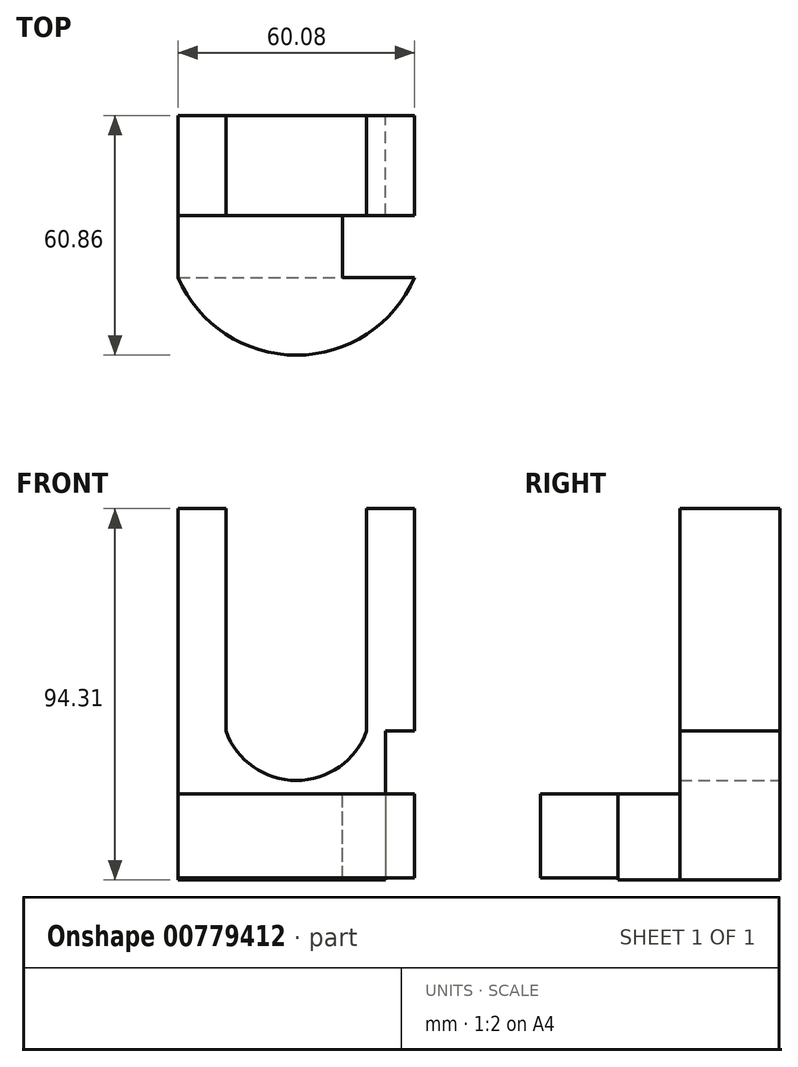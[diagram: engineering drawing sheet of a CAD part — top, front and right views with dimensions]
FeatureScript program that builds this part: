
annotation { "Feature Type Name" : "Feature", "Feature Type Description" : "" }
export const myFeature = defineFeature(function(context is Context, id is Id, definition is map)
    precondition{}
    {
        {
            var Q0;
            Q0=qCreatedBy(makeId("Front.planeOp"),FACE);
            var sketch = newSketch(context, id + "F0", { "sketchPlane" : qUnion([Q0])});
            skLineSegment(sketch, "E0.bottom", {"start": v(-60.08, 56.5) * mm, "end": v(-47.92, 56.5) * mm});
            skLineSegment(sketch, "E0.top", {"start": v(-60.08, -37.8) * mm, "end": v(0, -37.8) * mm});
            skLineSegment(sketch, "E0.left", {"start": v(-60.08, 56.5) * mm, "end": v(-60.08, -37.8) * mm});
            skLineSegment(sketch, "E0.right", {"start": v(0, 56.5) * mm, "end": v(0, -37.8) * mm});
            skLineSegment(sketch, "E1.left", {"start": v(-47.92, 56.5) * mm, "end": v(-47.92, 0) * mm});
            skLineSegment(sketch, "E1.right", {"start": v(-12.16, 56.5) * mm, "end": v(-12.16, 0) * mm});
            skLineSegment(sketch, "E2.trimOffspring", {"start": v(-12.16, 56.5) * mm, "end": v(0, 56.5) * mm});
            skArc(sketch, "E3", {"start": v(-47.92, 0) * mm, "mid": v(-30.04, -12.55) * mm, "end": v(-12.16, 0) * mm});
            skLineSegment(sketch, "E4.bottom", {"start": v(-60.08, -15.91) * mm, "end": v(0, -15.91) * mm});
            skLineSegment(sketch, "E4.left", {"start": v(-60.08, -15.91) * mm, "end": v(-60.08, -37.8) * mm});
            skLineSegment(sketch, "E4.right", {"start": v(0, -15.91) * mm, "end": v(0, -37.8) * mm});
            skSolve(sketch);
        }
        {
            var Q0;
            {var subQ4=sQuery(id+"F0.wireOp",EDGE,"E0.bottom");Q0=makeQuery(id+"F0.imprint","IMPRINT",FACE,{"disambiguationData":[TD([[makeQuery(id+"F0.imprint","IMPRINT",EDGE,{"derivedFrom":subQ4}),-1.0]])]});}
            extrude(context, id + "F1", {"entities" : qUnion([Q0]), "depth" : 25.4 * mm, "offsetDistance" : 25.4 * mm});
        }
        {
            var Q0;
            {var subQ0=sQuery(id+"F0.wireOp",EDGE,"E0.top");Q0=makeQuery(id+"F0.imprint","IMPRINT",FACE,{"disambiguationData":[TD([[makeQuery(id+"F0.imprint","IMPRINT",EDGE,{"derivedFrom":subQ0}),1.0]])]});}
            extrude(context, id + "F2", {"entities" : qUnion([Q0]), "operationType" : NewBodyOperationType.ADD, "depth" : 41.15 * mm, "offsetDistance" : 25.4 * mm});
        }
        {
            var Q0;
            Q0=makeQuery(id+"F2.opExtrude","SWEPT_FACE",FACE,{"disambiguationData":[OSD([sQuery(id+"F0.wireOp",EDGE,"E4.bottom")])]});
            var sketch = newSketch(context, id + "F3", { "sketchPlane" : qUnion([Q0])});
            skArc(sketch, "E5", {"start": v(-60.08, -41.15) * mm, "mid": v(-30.04, -60.86) * mm, "end": v(0, -41.15) * mm});
            skSolve(sketch);
        }
        {
            var Q0;
            Q0=makeQuery(id+"F3.imprint","IMPRINT",FACE,{"disambiguationData":[TD([[makeQuery(id+"F3.imprint","IMPRINT",EDGE,{"derivedFrom":sQuery(id+"F3.wireOp",EDGE,"E5")}),1.0]])]});
            extrude(context, id + "F4", {"entities" : qUnion([Q0]), "operationType" : NewBodyOperationType.ADD, "oppositeDirection" : true, "depth" : 21.34 * mm, "offsetDistance" : 25.4 * mm});
        }
        {
            var Q0;
            {var subQ0=sQuery(id+"F0.wireOp",EDGE,"E0.right");Q0=makeQuery(id+"F2.boolean.opBoolean","MERGE",FACE,{"derivedFrom":[makeQuery(id+"F1.opExtrude","SWEPT_FACE",FACE,{"disambiguationData":[OSD([subQ0])]}),makeQuery(id+"F2.opExtrude","SWEPT_FACE",FACE,{"disambiguationData":[OSD([subQ0])]})]});}
            var sketch = newSketch(context, id + "F5", { "sketchPlane" : qUnion([Q0])});
            skLineSegment(sketch, "E6.bottom", {"start": v(-25.4, 0) * mm, "end": v(0, 0) * mm});
            skLineSegment(sketch, "E6.top", {"start": v(-25.4, -37.8) * mm, "end": v(0, -37.8) * mm});
            skLineSegment(sketch, "E6.left", {"start": v(-25.4, 0) * mm, "end": v(-25.4, -37.8) * mm});
            skLineSegment(sketch, "E6.right", {"start": v(0, 0) * mm, "end": v(0, -37.8) * mm});
            skSolve(sketch);
        }
        {
            var Q0;
            {var subQ4=sQuery(id+"F5.wireOp",EDGE,"E6.bottom");Q0=makeQuery(id+"F5.imprint","IMPRINT",FACE,{"disambiguationData":[TD([[makeQuery(id+"F5.imprint","IMPRINT",EDGE,{"derivedFrom":subQ4}),-1.0]])]});}
            extrude(context, id + "F6", {"entities" : qUnion([Q0]), "operationType" : NewBodyOperationType.REMOVE, "oppositeDirection" : true, "depth" : 7.37 * mm, "offsetDistance" : 25.4 * mm});
        }
        {
            var Q0;
            {var subQ0=sQuery(id+"F0.wireOp",EDGE,"E4.bottom");Q0=makeQuery(id+"F4.boolean.opBoolean","MERGE",FACE,{"derivedFrom":[makeQuery(id+"F2.opExtrude","SWEPT_FACE",FACE,{"disambiguationData":[OSD([subQ0])]}),makeQuery(id+"F4.opExtrude","CAP_FACE",FACE,{"disambiguationData":[OSD([subQ0,sQuery(id+"F3.wireOp",EDGE,"E5")])],"isStart":true})]});}
            var sketch = newSketch(context, id + "F7", { "sketchPlane" : qUnion([Q0])});
            skLineSegment(sketch, "E7.bottom", {"start": v(-18.37, -25.4) * mm, "end": v(0, -25.4) * mm});
            skLineSegment(sketch, "E7.top", {"start": v(-18.37, -41.15) * mm, "end": v(0, -41.15) * mm});
            skLineSegment(sketch, "E7.left", {"start": v(-18.37, -25.4) * mm, "end": v(-18.37, -41.15) * mm});
            skLineSegment(sketch, "E7.right", {"start": v(0, -25.4) * mm, "end": v(0, -41.15) * mm});
            skSolve(sketch);
        }
        {
            var Q0;
            Q0=makeQuery(id+"F7.imprint","IMPRINT",FACE,{"disambiguationData":[TD([[makeQuery(id+"F7.imprint","IMPRINT",EDGE,{"derivedFrom":sQuery(id+"F7.wireOp",EDGE,"E7.top")}),1.0]])]});
            extrude(context, id + "F8", {"entities" : qUnion([Q0]), "operationType" : NewBodyOperationType.REMOVE, "endBound" : BoundingType.THROUGH_ALL, "oppositeDirection" : true, "depth" : 25.4 * mm, "offsetDistance" : 25.4 * mm});
        }
    });
